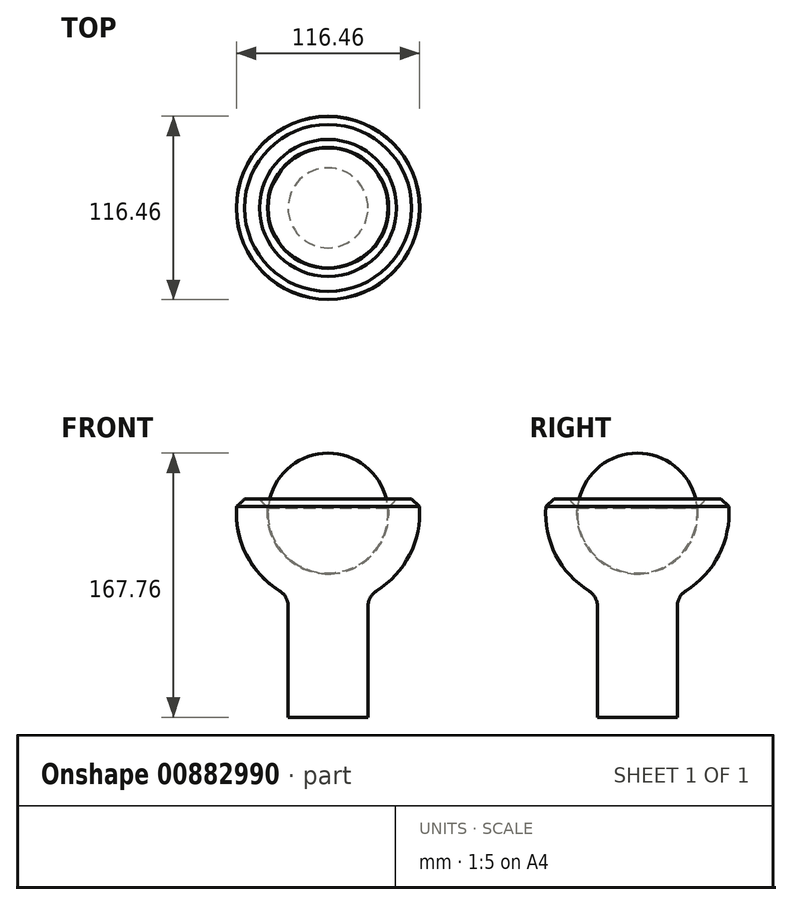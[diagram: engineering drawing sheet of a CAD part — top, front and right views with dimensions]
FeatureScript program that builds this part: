
annotation { "Feature Type Name" : "Feature", "Feature Type Description" : "" }
export const myFeature = defineFeature(function(context is Context, id is Id, definition is map)
    precondition{}
    {
        {
            var Q0;
            Q0=qCreatedBy(makeId("Top.planeOp"),FACE);
            var sketch = newSketch(context, id + "F0", { "sketchPlane" : qUnion([Q0])});
            skArc(sketch, "E0", {"start": v(0, 38.1) * mm, "mid": v(-38.1, 0) * mm, "end": v(0, -38.1) * mm});
            skLineSegment(sketch, "E1", {"start": v(0, 0) * mm, "end": v(0, 38.1) * mm});
            skLineSegment(sketch, "E2", {"start": v(0, 38.1) * mm, "end": v(0, 0) * mm});
            skLineSegment(sketch, "E3", {"start": v(0, 0) * mm, "end": v(0, -38.1) * mm});
            skSolve(sketch);
        }
        {
            var Q0;
            Q0 = qSketchRegion(id + "F0", true);
            var Q1;
            Q1=sQuery(id+"F0.wireOp",EDGE,"E1");
            revolve(context, id + "F1", {"surfaceOperationType" : NewSurfaceOperationType.NEW, "entities" : qUnion([Q0]), "axis" : qUnion([Q1]), "revolveType" : RevolveType.FULL});
        }
        {
            var Q0;
            Q0=qCreatedBy(makeId("Front.planeOp"),FACE);
            var sketch = newSketch(context, id + "F2", { "sketchPlane" : qUnion([Q0])});
            skArc(sketch, "E4", {"start": v(-37.57, 8.84) * mm, "mid": v(-30.26, -23.97) * mm, "end": v(0, -38.6) * mm});
            skArc(sketch, "E5", {"start": v(-57.56, 8.84) * mm, "mid": v(-44.2, -37.92) * mm, "end": v(0, -58.23) * mm});
            skLineSegment(sketch, "E6", {"start": v(-57.56, 8.84) * mm, "end": v(-37.57, 8.84) * mm});
            skCircle(sketch, "E7", {"center": v(0, 0) * mm, "radius": 38.1 * mm});
            skLineSegment(sketch, "E8.bottom", {"start": v(0, -129.66) * mm, "end": v(-25.4, -129.66) * mm});
            skLineSegment(sketch, "E8.right", {"start": v(-25.4, -129.66) * mm, "end": v(-25.4, -52.4) * mm});
            skPoint(sketch, "E8.middle", {"position": v(0, -58.23) * mm});
            skLineSegment(sketch, "E9.trimOffspring", {"start": v(-25.4, -29.07) * mm, "end": v(-25.4, -28.4) * mm});
            skLineSegment(sketch, "E10.trimOffspring", {"start": v(8.4, -37.68) * mm, "end": v(8.4, -37.16) * mm});
            skLineSegment(sketch, "E11", {"start": v(0, -38.6) * mm, "end": v(0, -129.66) * mm});
            skPoint(sketch, "E12.MirrorCS.start.orphan", {"position": v(57.56, 8.84) * mm});
            skPoint(sketch, "E13.orphan", {"position": v(25.4, -129.66) * mm});
            skPoint(sketch, "E14.trimOffspring.end.orphan", {"position": v(37.57, 8.84) * mm});
            skSolve(sketch);
        }
        {
            var Q0;
            {var subQ4=sQuery(id+"F2.wireOp",EDGE,"E8.bottom");Q0=makeQuery(id+"F2.imprint","IMPRINT",FACE,{"disambiguationData":[TD([[makeQuery(id+"F2.imprint","IMPRINT",EDGE,{"derivedFrom":subQ4}),-1.0]])]});}
            var Q1;
            {var subQ4=sQuery(id+"F2.wireOp",EDGE,"E6");Q1=makeQuery(id+"F2.imprint","IMPRINT",FACE,{"disambiguationData":[TD([[makeQuery(id+"F2.imprint","IMPRINT",EDGE,{"derivedFrom":subQ4}),-1.0]])]});}
            var Q2;
            Q2=sQuery(id+"F2.wireOp",EDGE,"E11");
            revolve(context, id + "F3", {"surfaceOperationType" : NewSurfaceOperationType.NEW, "entities" : qUnion([Q0, Q1]), "axis" : qUnion([Q2]), "revolveType" : RevolveType.FULL});
        }
        {
            var Q0;
            Q0=makeQuery(id+"F3.opRevolve","SWEPT_EDGE",EDGE,{"disambiguationData":[OSD([sQuery(id+"F2.wireOp",EDGE,"E4"),sQuery(id+"F2.wireOp",EDGE,"E6")])]});
            var Q1;
            Q1=makeQuery(id+"F3.opRevolve","SWEPT_EDGE",EDGE,{"disambiguationData":[OSD([sQuery(id+"F2.wireOp",EDGE,"E5"),sQuery(id+"F2.wireOp",EDGE,"E6")])]});
            chamfer(context, id + "F4", {"entities" : qUnion([Q0, Q1]), "width" : 5.08 * mm, "tangentPropagation" : true});
        }
        {
            var Q0;
            Q0=makeQuery(id+"F3.opRevolve","SWEPT_EDGE",EDGE,{"disambiguationData":[OSD([sQuery(id+"F2.wireOp",EDGE,"E5"),sQuery(id+"F2.wireOp",EDGE,"E8.right")])]});
            fillet(context, id + "F5", {"entities" : qUnion([Q0]), "radius" : 11.28 * mm, "tangentPropagation" : true, "allowEdgeOverflow" : false});
        }
    });
